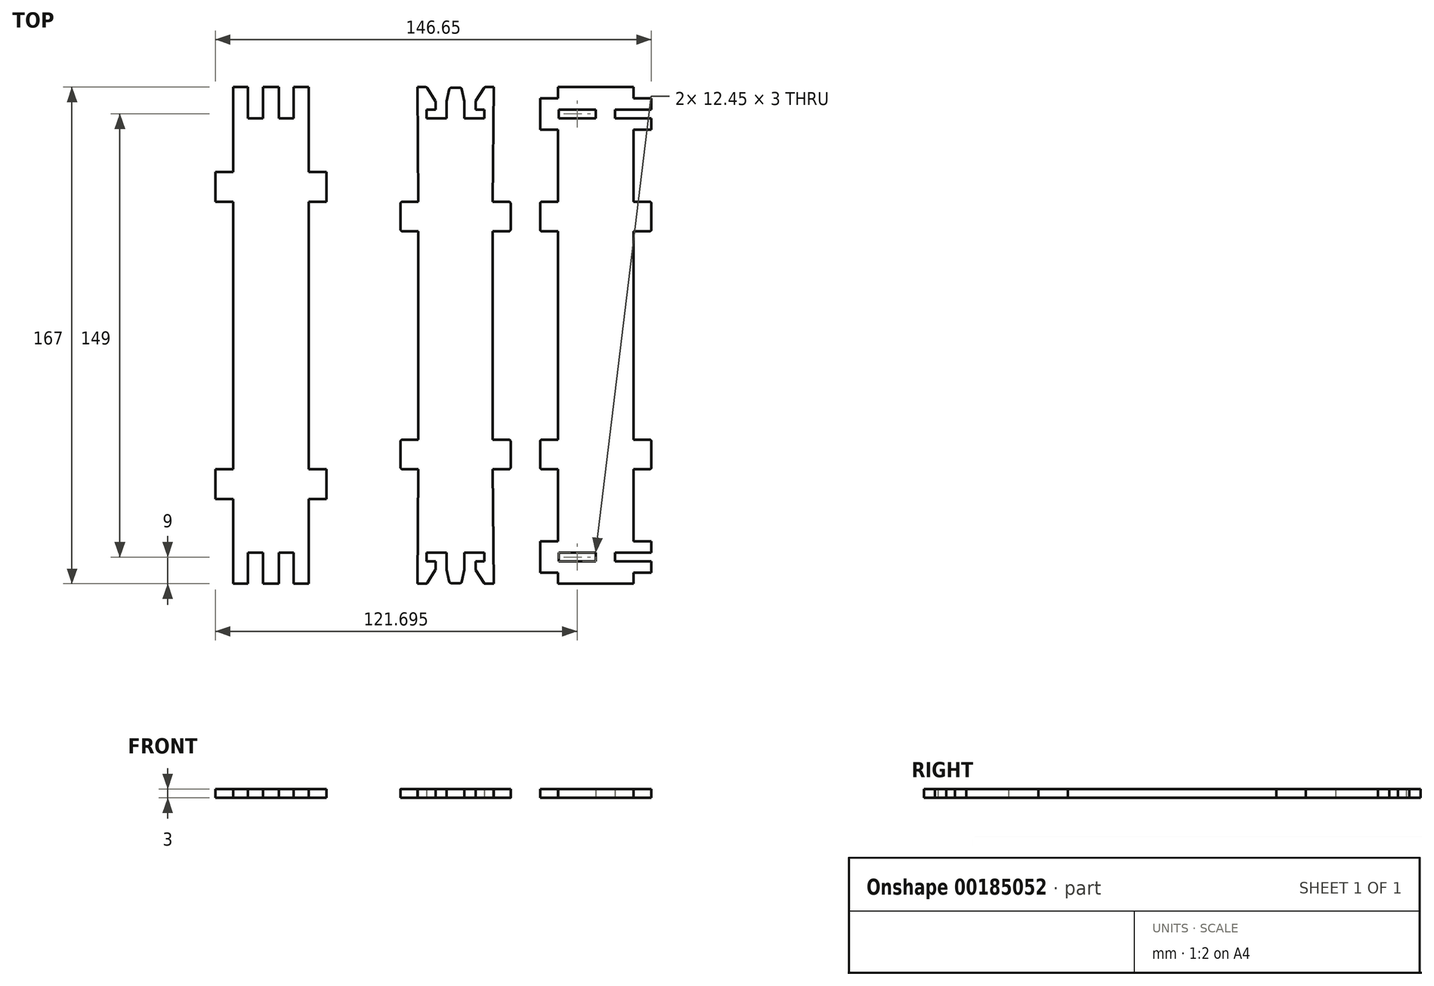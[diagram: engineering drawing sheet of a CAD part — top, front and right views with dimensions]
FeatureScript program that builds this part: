
annotation { "Feature Type Name" : "Feature", "Feature Type Description" : "" }
export const myFeature = defineFeature(function(context is Context, id is Id, definition is map)
    precondition{}
    {
        {
            var Q0;
            Q0=qCreatedBy(makeId("Top.planeOp"),FACE);
            var sketch = newSketch(context, id + "F0", { "sketchPlane" : qUnion([Q0])});
            skLineSegment(sketch, "E0.MirrorCS", {"start": v(-9.7, 76) * mm, "end": v(-6.7, 76) * mm});
            skLineSegment(sketch, "E1.MirrorCS", {"start": v(-6.7, 76) * mm, "end": v(-6.7, 78.56) * mm});
            skLineSegment(sketch, "E2.MirrorCS", {"start": v(-3, 78.75) * mm, "end": v(-3, 73) * mm});
            skLineSegment(sketch, "E3.MirrorCS", {"start": v(-9.7, 76) * mm, "end": v(-9.7, 73) * mm});
            skLineSegment(sketch, "E4.MirrorCS", {"start": v(-9.7, 73) * mm, "end": v(-7.7, 48) * mm});
            skLineSegment(sketch, "E5.MirrorCS", {"start": v(-3, 78.75) * mm, "end": v(-2.1, 82.76) * mm});
            skLineSegment(sketch, "E6.MirrorCS", {"start": v(-3, 73) * mm, "end": v(-9.7, 73) * mm});
            skLineSegment(sketch, "E7", {"start": v(-1.46, 83.28) * mm, "end": v(0, 83.28) * mm});
            skArc(sketch, "E8.filletArc", {"start": v(-1.46, 83.28) * mm, "mid": v(-1.87, 83.14) * mm, "end": v(-2.1, 82.76) * mm});
            skLineSegment(sketch, "E9", {"start": v(-12.78, 83.5) * mm, "end": v(-10.06, 83.5) * mm});
            skLineSegment(sketch, "E10", {"start": v(-9.5, 83.2) * mm, "end": v(-6.8, 78.9) * mm});
            skPoint(sketch, "E11.visualSharp", {"position": v(-9.7, 83.5) * mm});
            skArc(sketch, "E11.filletArc", {"start": v(-9.5, 83.2) * mm, "mid": v(-9.75, 83.42) * mm, "end": v(-10.06, 83.5) * mm});
            skPoint(sketch, "E12.visualSharp", {"position": v(-6.7, 78.75) * mm});
            skArc(sketch, "E12.filletArc", {"start": v(-6.7, 78.56) * mm, "mid": v(-6.73, 78.74) * mm, "end": v(-6.8, 78.9) * mm});
            skLineSegment(sketch, "E13", {"start": v(-12.5, 35) * mm, "end": v(-17.84, 35) * mm});
            skLineSegment(sketch, "E14", {"start": v(-18.5, 35.66) * mm, "end": v(-18.5, 44.34) * mm});
            skLineSegment(sketch, "E15", {"start": v(-17.84, 45) * mm, "end": v(-12.5, 45) * mm});
            skLineSegment(sketch, "E16", {"start": v(-12.5, 35) * mm, "end": v(-12.5, 0) * mm});
            skPoint(sketch, "E17.visualSharp", {"position": v(-18.5, 45) * mm});
            skArc(sketch, "E17.filletArc", {"start": v(-17.84, 45) * mm, "mid": v(-18.3, 44.8) * mm, "end": v(-18.5, 44.34) * mm});
            skPoint(sketch, "E18.visualSharp", {"position": v(-18.5, 35) * mm});
            skArc(sketch, "E18.filletArc", {"start": v(-18.5, 35.66) * mm, "mid": v(-18.3, 35.2) * mm, "end": v(-17.84, 35) * mm});
            skLineSegment(sketch, "E19", {"start": v(-12.78, 83.5) * mm, "end": v(-12.5, 45) * mm});
            skArc(sketch, "E20.MirrorCS", {"start": v(6.7, 78.56) * mm, "mid": v(6.73, 78.74) * mm, "end": v(6.8, 78.9) * mm});
            skArc(sketch, "E21.MirrorCS", {"start": v(18.5, 35.66) * mm, "mid": v(18.3, 35.2) * mm, "end": v(17.84, 35) * mm});
            skLineSegment(sketch, "E22.MirrorCS", {"start": v(1.46, 83.28) * mm, "end": v(0, 83.28) * mm});
            skArc(sketch, "E23.MirrorCS", {"start": v(1.46, 83.28) * mm, "mid": v(1.87, 83.14) * mm, "end": v(2.1, 82.76) * mm});
            skLineSegment(sketch, "E24.MirrorCS", {"start": v(9.5, 83.2) * mm, "end": v(6.8, 78.9) * mm});
            skArc(sketch, "E25.MirrorCS", {"start": v(9.5, 83.2) * mm, "mid": v(9.75, 83.42) * mm, "end": v(10.06, 83.5) * mm});
            skArc(sketch, "E26.MirrorCS", {"start": v(17.84, 45) * mm, "mid": v(18.3, 44.8) * mm, "end": v(18.5, 44.34) * mm});
            skLineSegment(sketch, "E27.MirrorCS", {"start": v(3, 78.75) * mm, "end": v(2.1, 82.76) * mm});
            skLineSegment(sketch, "E28.MirrorCS", {"start": v(12.78, 83.5) * mm, "end": v(10.06, 83.5) * mm});
            skLineSegment(sketch, "E29.MirrorCS", {"start": v(12.5, 35) * mm, "end": v(17.84, 35) * mm});
            skLineSegment(sketch, "E30.MirrorCS", {"start": v(6.7, 76) * mm, "end": v(6.7, 78.56) * mm});
            skLineSegment(sketch, "E31.MirrorCS", {"start": v(9.7, 76) * mm, "end": v(9.7, 73) * mm});
            skLineSegment(sketch, "E32.MirrorCS", {"start": v(9.7, 76) * mm, "end": v(6.7, 76) * mm});
            skLineSegment(sketch, "E33.MirrorCS", {"start": v(17.84, 45) * mm, "end": v(12.5, 45) * mm});
            skLineSegment(sketch, "E34.MirrorCS", {"start": v(9.7, 73) * mm, "end": v(7.7, 48) * mm});
            skPoint(sketch, "E35.MirrorP", {"position": v(18.5, 35) * mm});
            skPoint(sketch, "E36.MirrorP", {"position": v(18.5, 45) * mm});
            skLineSegment(sketch, "E37.MirrorCS", {"start": v(3, 73) * mm, "end": v(9.7, 73) * mm});
            skPoint(sketch, "E38.MirrorP", {"position": v(6.7, 78.75) * mm});
            skLineSegment(sketch, "E39.MirrorCS", {"start": v(3, 78.75) * mm, "end": v(3, 73) * mm});
            skLineSegment(sketch, "E40.MirrorCS", {"start": v(18.5, 35.66) * mm, "end": v(18.5, 44.34) * mm});
            skLineSegment(sketch, "E41.MirrorCS", {"start": v(12.78, 83.5) * mm, "end": v(12.5, 45) * mm});
            skLineSegment(sketch, "E42.MirrorCS", {"start": v(12.5, 35) * mm, "end": v(12.5, 0) * mm});
            skPoint(sketch, "E43.MirrorP", {"position": v(9.7, 83.5) * mm});
            skArc(sketch, "E44.MirrorCS", {"start": v(-6.7, -78.56) * mm, "mid": v(-6.73, -78.74) * mm, "end": v(-6.8, -78.9) * mm});
            skLineSegment(sketch, "E45.MirrorCS", {"start": v(-6.7, -76) * mm, "end": v(-6.7, -78.56) * mm});
            skArc(sketch, "E46.MirrorCS", {"start": v(17.84, -45) * mm, "mid": v(18.3, -44.8) * mm, "end": v(18.5, -44.34) * mm});
            skArc(sketch, "E47.MirrorCS", {"start": v(-17.84, -45) * mm, "mid": v(-18.3, -44.8) * mm, "end": v(-18.5, -44.34) * mm});
            skLineSegment(sketch, "E48.MirrorCS", {"start": v(-9.7, -76) * mm, "end": v(-6.7, -76) * mm});
            skLineSegment(sketch, "E49.MirrorCS", {"start": v(-9.7, -76) * mm, "end": v(-9.7, -73) * mm});
            skArc(sketch, "E50.MirrorCS", {"start": v(6.7, -78.56) * mm, "mid": v(6.73, -78.74) * mm, "end": v(6.8, -78.9) * mm});
            skLineSegment(sketch, "E51.MirrorCS", {"start": v(6.7, -76) * mm, "end": v(6.7, -78.56) * mm});
            skLineSegment(sketch, "E52.MirrorCS", {"start": v(9.7, -76) * mm, "end": v(9.7, -73) * mm});
            skArc(sketch, "E53.MirrorCS", {"start": v(-9.5, -83.2) * mm, "mid": v(-9.75, -83.42) * mm, "end": v(-10.06, -83.5) * mm});
            skArc(sketch, "E54.MirrorCS", {"start": v(-18.5, -35.66) * mm, "mid": v(-18.3, -35.2) * mm, "end": v(-17.84, -35) * mm});
            skArc(sketch, "E55.MirrorCS", {"start": v(18.5, -35.66) * mm, "mid": v(18.3, -35.2) * mm, "end": v(17.84, -35) * mm});
            skLineSegment(sketch, "E56.MirrorCS", {"start": v(12.78, -83.5) * mm, "end": v(10.06, -83.5) * mm});
            skArc(sketch, "E57.MirrorCS", {"start": v(9.5, -83.2) * mm, "mid": v(9.75, -83.42) * mm, "end": v(10.06, -83.5) * mm});
            skArc(sketch, "E58.MirrorCS", {"start": v(-1.46, -83.28) * mm, "mid": v(-1.87, -83.14) * mm, "end": v(-2.1, -82.76) * mm});
            skLineSegment(sketch, "E59.MirrorCS", {"start": v(-1.46, -83.28) * mm, "end": v(0, -83.28) * mm});
            skLineSegment(sketch, "E60.MirrorCS", {"start": v(1.46, -83.28) * mm, "end": v(0, -83.28) * mm});
            skArc(sketch, "E61.MirrorCS", {"start": v(1.46, -83.28) * mm, "mid": v(1.87, -83.14) * mm, "end": v(2.1, -82.76) * mm});
            skLineSegment(sketch, "E62.MirrorCS", {"start": v(-12.78, -83.5) * mm, "end": v(-10.06, -83.5) * mm});
            skLineSegment(sketch, "E63.MirrorCS", {"start": v(-9.5, -83.2) * mm, "end": v(-6.8, -78.9) * mm});
            skLineSegment(sketch, "E64.MirrorCS", {"start": v(9.5, -83.2) * mm, "end": v(6.8, -78.9) * mm});
            skLineSegment(sketch, "E65.MirrorCS", {"start": v(3, -78.75) * mm, "end": v(2.1, -82.76) * mm});
            skLineSegment(sketch, "E66.MirrorCS", {"start": v(-3, -78.75) * mm, "end": v(-2.1, -82.76) * mm});
            skLineSegment(sketch, "E67.MirrorCS", {"start": v(-17.84, -45) * mm, "end": v(-12.5, -45) * mm});
            skLineSegment(sketch, "E68.MirrorCS", {"start": v(12.5, -35) * mm, "end": v(17.84, -35) * mm});
            skLineSegment(sketch, "E69.MirrorCS", {"start": v(-3, -78.75) * mm, "end": v(-3, -73) * mm});
            skLineSegment(sketch, "E70.MirrorCS", {"start": v(-12.5, -35) * mm, "end": v(-17.84, -35) * mm});
            skLineSegment(sketch, "E71.MirrorCS", {"start": v(3, -78.75) * mm, "end": v(3, -73) * mm});
            skLineSegment(sketch, "E72.MirrorCS", {"start": v(17.84, -45) * mm, "end": v(12.5, -45) * mm});
            skLineSegment(sketch, "E73.MirrorCS", {"start": v(9.7, -76) * mm, "end": v(6.7, -76) * mm});
            skLineSegment(sketch, "E74.MirrorCS", {"start": v(-9.7, -73) * mm, "end": v(-7.7, -48) * mm});
            skLineSegment(sketch, "E75.MirrorCS", {"start": v(9.7, -73) * mm, "end": v(7.7, -48) * mm});
            skLineSegment(sketch, "E76.MirrorCS", {"start": v(3, -73) * mm, "end": v(9.7, -73) * mm});
            skPoint(sketch, "E77.MirrorP", {"position": v(18.5, -35) * mm});
            skLineSegment(sketch, "E78.MirrorCS", {"start": v(18.5, -35.66) * mm, "end": v(18.5, -44.34) * mm});
            skLineSegment(sketch, "E79.MirrorCS", {"start": v(12.5, -35) * mm, "end": v(12.5, 0) * mm});
            skPoint(sketch, "E80.MirrorP", {"position": v(-18.5, -35) * mm});
            skPoint(sketch, "E81.MirrorP", {"position": v(-9.7, -83.5) * mm});
            skPoint(sketch, "E82.MirrorP", {"position": v(6.7, -78.75) * mm});
            skPoint(sketch, "E83.MirrorP", {"position": v(-18.5, -45) * mm});
            skLineSegment(sketch, "E84.MirrorCS", {"start": v(-12.78, -83.5) * mm, "end": v(-12.5, -45) * mm});
            skLineSegment(sketch, "E85.MirrorCS", {"start": v(-18.5, -35.66) * mm, "end": v(-18.5, -44.34) * mm});
            skPoint(sketch, "E86.MirrorP", {"position": v(18.5, -45) * mm});
            skPoint(sketch, "E87.MirrorP", {"position": v(-6.7, -78.75) * mm});
            skLineSegment(sketch, "E88.MirrorCS", {"start": v(-12.5, -35) * mm, "end": v(-12.5, 0) * mm});
            skLineSegment(sketch, "E89.MirrorCS", {"start": v(-3, -73) * mm, "end": v(-9.7, -73) * mm});
            skLineSegment(sketch, "E90.MirrorCS", {"start": v(12.78, -83.5) * mm, "end": v(12.5, -45) * mm});
            skPoint(sketch, "E91.MirrorP", {"position": v(9.7, -83.5) * mm});
            skSolve(sketch);
        }
        {
            var Q0;
            Q0=qSketchRegion(id+"F0",true);
            extrude(context, id + "F1", {"entities" : qUnion([Q0]), "depth" : 3 * mm});
        }
        {
            var Q0;
            Q0=qCreatedBy(makeId("Top.planeOp"),FACE);
            var sketch = newSketch(context, id + "F2", { "sketchPlane" : qUnion([Q0])});
            skLineSegment(sketch, "E92.0", {"start": v(29.09, 45) * mm, "end": v(34.43, 45) * mm});
            skLineSegment(sketch, "E93.0", {"start": v(28.43, 35.66) * mm, "end": v(28.43, 44.34) * mm});
            skArc(sketch, "E94.0", {"start": v(29.09, 45) * mm, "mid": v(28.62, 44.8) * mm, "end": v(28.43, 44.34) * mm});
            skArc(sketch, "E95.0", {"start": v(28.43, 35.66) * mm, "mid": v(28.62, 35.2) * mm, "end": v(29.09, 35) * mm});
            skLineSegment(sketch, "E96.0", {"start": v(34.43, 35) * mm, "end": v(29.09, 35) * mm});
            skLineSegment(sketch, "E97", {"start": v(34.43, 45) * mm, "end": v(34.43, 69.25) * mm});
            skLineSegment(sketch, "E98", {"start": v(34.43, 69.25) * mm, "end": v(28.43, 69.25) * mm});
            skLineSegment(sketch, "E99", {"start": v(28.43, 69.25) * mm, "end": v(28.43, 79.75) * mm});
            skLineSegment(sketch, "E100", {"start": v(34.65, 73) * mm, "end": v(47.1, 73) * mm});
            skLineSegment(sketch, "E101", {"start": v(65.83, 73) * mm, "end": v(65.83, 69.25) * mm});
            skArc(sketch, "E102.MirrorCS", {"start": v(65.83, 35.66) * mm, "mid": v(65.63, 35.2) * mm, "end": v(65.16, 35) * mm});
            skArc(sketch, "E103.MirrorCS", {"start": v(65.16, 45) * mm, "mid": v(65.63, 44.8) * mm, "end": v(65.83, 44.34) * mm});
            skLineSegment(sketch, "E104.MirrorCS", {"start": v(59.83, 35) * mm, "end": v(65.16, 35) * mm});
            skLineSegment(sketch, "E105.MirrorCS", {"start": v(65.16, 45) * mm, "end": v(59.83, 45) * mm});
            skLineSegment(sketch, "E106.MirrorCS", {"start": v(65.83, 35.66) * mm, "end": v(65.83, 44.34) * mm});
            skLineSegment(sketch, "E107.MirrorCS", {"start": v(59.83, 45) * mm, "end": v(59.83, 69.25) * mm});
            skLineSegment(sketch, "E108", {"start": v(34.43, 35) * mm, "end": v(34.43, 0) * mm});
            skLineSegment(sketch, "E109", {"start": v(59.83, 35) * mm, "end": v(59.83, 0) * mm});
            skLineSegment(sketch, "E110", {"start": v(47.1, 76) * mm, "end": v(47.1, 73) * mm});
            skLineSegment(sketch, "E111", {"start": v(34.65, 76) * mm, "end": v(34.65, 73) * mm});
            skLineSegment(sketch, "E112", {"start": v(59.83, 69.25) * mm, "end": v(65.83, 69.25) * mm});
            skLineSegment(sketch, "E113", {"start": v(34.65, 76) * mm, "end": v(47.1, 76) * mm});
            skLineSegment(sketch, "E114", {"start": v(28.43, 79.75) * mm, "end": v(34.44, 79.75) * mm});
            skLineSegment(sketch, "E115", {"start": v(34.44, 79.75) * mm, "end": v(34.44, 83.5) * mm});
            skLineSegment(sketch, "E116", {"start": v(34.44, 83.5) * mm, "end": v(59.83, 83.5) * mm});
            skLineSegment(sketch, "E117", {"start": v(59.83, 83.5) * mm, "end": v(59.83, 79.75) * mm});
            skLineSegment(sketch, "E118", {"start": v(59.83, 79.75) * mm, "end": v(65.83, 79.75) * mm});
            skLineSegment(sketch, "E119", {"start": v(65.83, 79.75) * mm, "end": v(65.83, 76) * mm});
            skLineSegment(sketch, "E120", {"start": v(65.83, 76) * mm, "end": v(53.6, 76) * mm});
            skLineSegment(sketch, "E121", {"start": v(53.6, 76) * mm, "end": v(53.6, 73) * mm});
            skLineSegment(sketch, "E122", {"start": v(53.6, 73) * mm, "end": v(65.83, 73) * mm});
            skArc(sketch, "E123.MirrorCS", {"start": v(29.09, -45) * mm, "mid": v(28.62, -44.8) * mm, "end": v(28.43, -44.34) * mm});
            skLineSegment(sketch, "E124.MirrorCS", {"start": v(65.83, -73) * mm, "end": v(65.83, -69.25) * mm});
            skLineSegment(sketch, "E125.MirrorCS", {"start": v(53.6, -76) * mm, "end": v(53.6, -73) * mm});
            skLineSegment(sketch, "E126.MirrorCS", {"start": v(65.83, -79.75) * mm, "end": v(65.83, -76) * mm});
            skLineSegment(sketch, "E127.MirrorCS", {"start": v(28.43, -79.75) * mm, "end": v(34.44, -79.75) * mm});
            skLineSegment(sketch, "E128.MirrorCS", {"start": v(34.44, -79.75) * mm, "end": v(34.44, -83.5) * mm});
            skLineSegment(sketch, "E129.MirrorCS", {"start": v(65.16, -45) * mm, "end": v(59.83, -45) * mm});
            skArc(sketch, "E130.MirrorCS", {"start": v(28.43, -35.66) * mm, "mid": v(28.62, -35.2) * mm, "end": v(29.09, -35) * mm});
            skLineSegment(sketch, "E131.MirrorCS", {"start": v(34.43, -35) * mm, "end": v(29.09, -35) * mm});
            skArc(sketch, "E132.MirrorCS", {"start": v(65.16, -45) * mm, "mid": v(65.63, -44.8) * mm, "end": v(65.83, -44.34) * mm});
            skArc(sketch, "E133.MirrorCS", {"start": v(65.83, -35.66) * mm, "mid": v(65.63, -35.2) * mm, "end": v(65.16, -35) * mm});
            skLineSegment(sketch, "E134.MirrorCS", {"start": v(34.43, -69.25) * mm, "end": v(28.43, -69.25) * mm});
            skLineSegment(sketch, "E135.MirrorCS", {"start": v(34.65, -76) * mm, "end": v(34.65, -73) * mm});
            skLineSegment(sketch, "E136.MirrorCS", {"start": v(59.83, -69.25) * mm, "end": v(65.83, -69.25) * mm});
            skLineSegment(sketch, "E137.MirrorCS", {"start": v(59.83, -83.5) * mm, "end": v(59.83, -79.75) * mm});
            skLineSegment(sketch, "E138.MirrorCS", {"start": v(29.09, -45) * mm, "end": v(34.43, -45) * mm});
            skLineSegment(sketch, "E139.MirrorCS", {"start": v(47.1, -76) * mm, "end": v(47.1, -73) * mm});
            skLineSegment(sketch, "E140.MirrorCS", {"start": v(59.83, -79.75) * mm, "end": v(65.83, -79.75) * mm});
            skLineSegment(sketch, "E141.MirrorCS", {"start": v(59.83, -35) * mm, "end": v(65.16, -35) * mm});
            skLineSegment(sketch, "E142.MirrorCS", {"start": v(65.83, -76) * mm, "end": v(53.6, -76) * mm});
            skLineSegment(sketch, "E143.MirrorCS", {"start": v(53.6, -73) * mm, "end": v(65.83, -73) * mm});
            skLineSegment(sketch, "E144.MirrorCS", {"start": v(59.83, -45) * mm, "end": v(59.83, -69.25) * mm});
            skLineSegment(sketch, "E145.MirrorCS", {"start": v(34.65, -76) * mm, "end": v(47.1, -76) * mm});
            skLineSegment(sketch, "E146.MirrorCS", {"start": v(34.43, -35) * mm, "end": v(34.43, 0) * mm});
            skLineSegment(sketch, "E147.MirrorCS", {"start": v(34.44, -83.5) * mm, "end": v(59.83, -83.5) * mm});
            skLineSegment(sketch, "E148.MirrorCS", {"start": v(65.83, -35.66) * mm, "end": v(65.83, -44.34) * mm});
            skLineSegment(sketch, "E149.MirrorCS", {"start": v(59.83, -35) * mm, "end": v(59.83, 0) * mm});
            skLineSegment(sketch, "E150.MirrorCS", {"start": v(34.43, -45) * mm, "end": v(34.43, -69.25) * mm});
            skLineSegment(sketch, "E151.MirrorCS", {"start": v(28.43, -69.25) * mm, "end": v(28.43, -79.75) * mm});
            skLineSegment(sketch, "E152.MirrorCS", {"start": v(28.43, -35.66) * mm, "end": v(28.43, -44.34) * mm});
            skLineSegment(sketch, "E153.MirrorCS", {"start": v(34.65, -73) * mm, "end": v(47.1, -73) * mm});
            skSolve(sketch);
        }
        {
            var Q0;
            Q0 = qSketchRegion(id + "F2", true);
            extrude(context, id + "F3", {"entities" : qUnion([Q0]), "depth" : 3 * mm});
        }
        {
            var Q0;
            Q0=qCreatedBy(makeId("Top.planeOp"),FACE);
            var sketch = newSketch(context, id + "F4", { "sketchPlane" : qUnion([Q0])});
            skLineSegment(sketch, "E154", {"start": v(-74.82, 0) * mm, "end": v(-74.82, 45) * mm});
            skLineSegment(sketch, "E155", {"start": v(-74.82, 45) * mm, "end": v(-80.82, 45) * mm});
            skLineSegment(sketch, "E156", {"start": v(-80.82, 45) * mm, "end": v(-80.82, 55) * mm});
            skLineSegment(sketch, "E157", {"start": v(-80.82, 55) * mm, "end": v(-74.82, 55) * mm});
            skLineSegment(sketch, "E158", {"start": v(-74.82, 55) * mm, "end": v(-74.82, 83.5) * mm});
            skLineSegment(sketch, "E159", {"start": v(-74.82, 83.5) * mm, "end": v(-69.82, 83.5) * mm});
            skLineSegment(sketch, "E160", {"start": v(-69.82, 83.5) * mm, "end": v(-69.82, 73) * mm});
            skLineSegment(sketch, "E161", {"start": v(-69.82, 73) * mm, "end": v(-64.82, 73) * mm});
            skLineSegment(sketch, "E162", {"start": v(-64.82, 73) * mm, "end": v(-64.82, 83.5) * mm});
            skLineSegment(sketch, "E163", {"start": v(-64.82, 83.5) * mm, "end": v(-59.42, 83.5) * mm});
            skLineSegment(sketch, "E164", {"start": v(-59.42, 83.5) * mm, "end": v(-59.42, 73) * mm});
            skLineSegment(sketch, "E165", {"start": v(-59.42, 73) * mm, "end": v(-54.42, 73) * mm});
            skLineSegment(sketch, "E166", {"start": v(-54.42, 73) * mm, "end": v(-54.42, 83.5) * mm});
            skLineSegment(sketch, "E167", {"start": v(-54.42, 83.5) * mm, "end": v(-49.42, 83.5) * mm});
            skLineSegment(sketch, "E168", {"start": v(-49.42, 83.5) * mm, "end": v(-49.42, 55) * mm});
            skLineSegment(sketch, "E169", {"start": v(-49.42, 55) * mm, "end": v(-43.42, 55) * mm});
            skLineSegment(sketch, "E170", {"start": v(-43.42, 55) * mm, "end": v(-43.42, 45) * mm});
            skLineSegment(sketch, "E171", {"start": v(-43.42, 45) * mm, "end": v(-49.42, 45) * mm});
            skLineSegment(sketch, "E172", {"start": v(-49.42, 45) * mm, "end": v(-49.42, 0) * mm});
            skLineSegment(sketch, "E173.MirrorCS", {"start": v(-59.42, -83.5) * mm, "end": v(-59.42, -73) * mm});
            skLineSegment(sketch, "E174.MirrorCS", {"start": v(-59.42, -73) * mm, "end": v(-54.42, -73) * mm});
            skLineSegment(sketch, "E175.MirrorCS", {"start": v(-69.82, -73) * mm, "end": v(-64.82, -73) * mm});
            skLineSegment(sketch, "E176.MirrorCS", {"start": v(-80.82, -55) * mm, "end": v(-74.82, -55) * mm});
            skLineSegment(sketch, "E177.MirrorCS", {"start": v(-43.42, -45) * mm, "end": v(-49.42, -45) * mm});
            skLineSegment(sketch, "E178.MirrorCS", {"start": v(-54.42, -83.5) * mm, "end": v(-49.42, -83.5) * mm});
            skLineSegment(sketch, "E179.MirrorCS", {"start": v(-74.82, -45) * mm, "end": v(-80.82, -45) * mm});
            skLineSegment(sketch, "E180.MirrorCS", {"start": v(-74.82, -83.5) * mm, "end": v(-69.82, -83.5) * mm});
            skLineSegment(sketch, "E181.MirrorCS", {"start": v(-54.42, -73) * mm, "end": v(-54.42, -83.5) * mm});
            skLineSegment(sketch, "E182.MirrorCS", {"start": v(-49.42, -55) * mm, "end": v(-43.42, -55) * mm});
            skLineSegment(sketch, "E183.MirrorCS", {"start": v(-64.82, -73) * mm, "end": v(-64.82, -83.5) * mm});
            skLineSegment(sketch, "E184.MirrorCS", {"start": v(-69.82, -83.5) * mm, "end": v(-69.82, -73) * mm});
            skLineSegment(sketch, "E185.MirrorCS", {"start": v(-64.82, -83.5) * mm, "end": v(-59.42, -83.5) * mm});
            skLineSegment(sketch, "E186.MirrorCS", {"start": v(-49.42, -83.5) * mm, "end": v(-49.42, -55) * mm});
            skLineSegment(sketch, "E187.MirrorCS", {"start": v(-80.82, -45) * mm, "end": v(-80.82, -55) * mm});
            skLineSegment(sketch, "E188.MirrorCS", {"start": v(-49.42, -45) * mm, "end": v(-49.42, 0) * mm});
            skLineSegment(sketch, "E189.MirrorCS", {"start": v(-74.82, -55) * mm, "end": v(-74.82, -83.5) * mm});
            skLineSegment(sketch, "E190.MirrorCS", {"start": v(-74.82, 0) * mm, "end": v(-74.82, -45) * mm});
            skLineSegment(sketch, "E191.MirrorCS", {"start": v(-43.42, -55) * mm, "end": v(-43.42, -45) * mm});
            skSolve(sketch);
        }
        {
            var Q0;
            Q0=makeQuery(id+"F4.imprint","IMPRINT",FACE,{"disambiguationData":[TD([[makeQuery(id+"F4.imprint","IMPRINT",EDGE,{"derivedFrom":sQuery(id+"F4.wireOp",EDGE,"E154")}),-1.0]])]});
            extrude(context, id + "F5", {"entities" : qUnion([Q0]), "depth" : 3 * mm});
        }
    });
